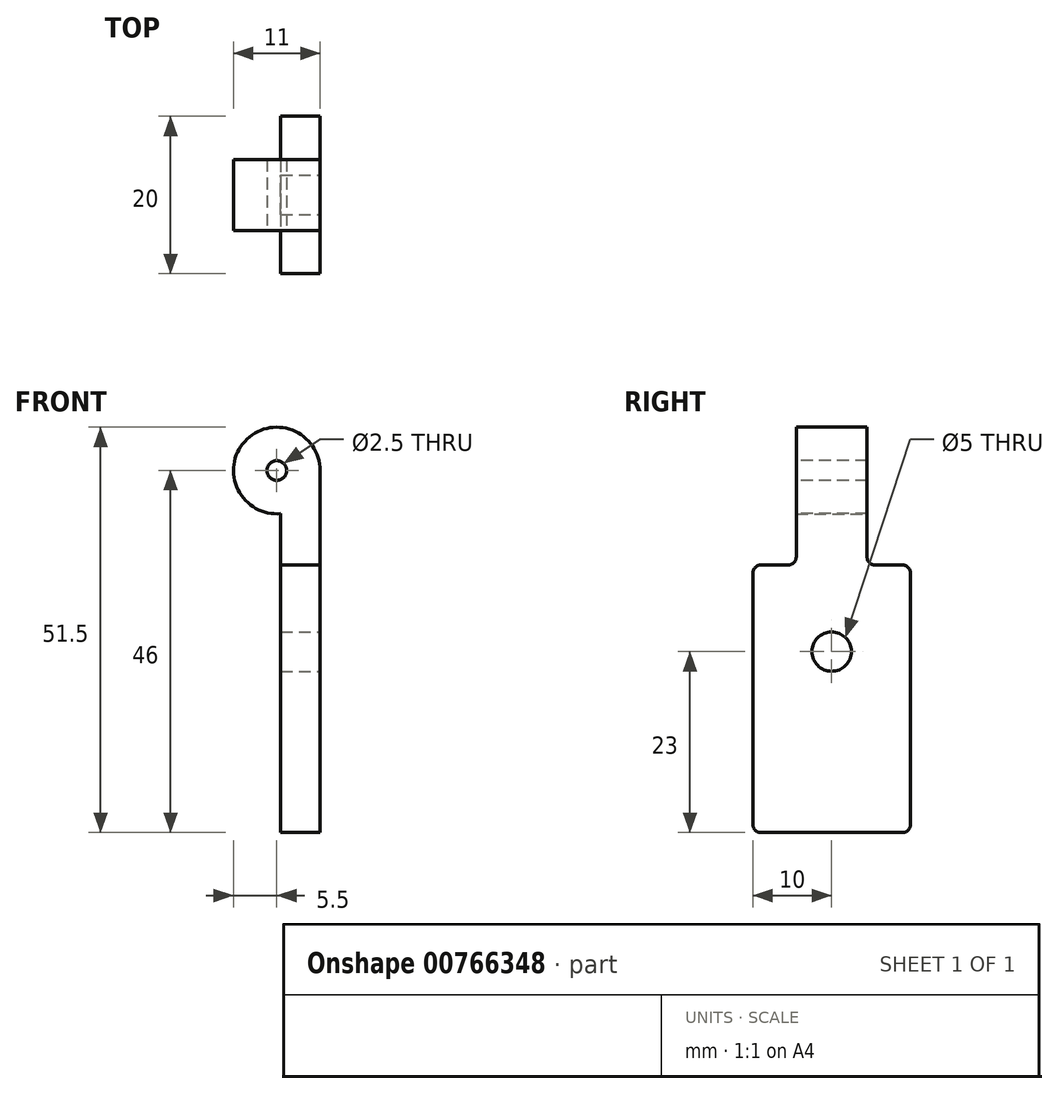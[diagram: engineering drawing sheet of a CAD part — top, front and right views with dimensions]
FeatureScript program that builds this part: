
annotation { "Feature Type Name" : "Feature", "Feature Type Description" : "" }
export const myFeature = defineFeature(function(context is Context, id is Id, definition is map)
    precondition{}
    {
        {
            var Q0;
            Q0=qCreatedBy(makeId("Front.planeOp"),FACE);
            var sketch = newSketch(context, id + "F0", { "sketchPlane" : qUnion([Q0])});
            skCircle(sketch, "E0", {"center": v(0, 0) * mm, "radius": 5.5 * mm});
            skSolve(sketch);
        }
        {
            var Q0;
            Q0 = qSketchRegion(id + "F0", true);
            extrude(context, id + "F1", {"entities" : qUnion([Q0]), "endBound" : BoundingType.SYMMETRIC, "depth" : 9 * mm, "offsetDistance" : 25 * mm});
        }
        {
            var Q0;
            Q0=makeQuery(id+"F1.opExtrude","CAP_FACE",FACE,{"disambiguationData":[OSD([sQuery(id+"F0.wireOp",EDGE,"E0")])],"isStart":false});
            var sketch = newSketch(context, id + "F2", { "sketchPlane" : qUnion([Q0])});
            skLineSegment(sketch, "E1", {"start": v(5.5, 0) * mm, "end": v(5.5, -46) * mm});
            skLineSegment(sketch, "E2", {"start": v(5.5, -46) * mm, "end": v(0.5, -46) * mm});
            skLineSegment(sketch, "E3", {"start": v(0.5, -46) * mm, "end": v(0.5, -5.48) * mm});
            skArc(sketch, "E4.0", {"start": v(0.5, -5.48) * mm, "mid": v(4.06, -3.7) * mm, "end": v(5.5, 0) * mm});
            skSolve(sketch);
        }
        {
            var Q0;
            Q0 = qSketchRegion(id + "F2", true);
            var Q1;
            Q1=makeQuery(id+"F1.opExtrude","CAP_FACE",FACE,{"disambiguationData":[OSD([sQuery(id+"F0.wireOp",EDGE,"E0")])],"isStart":true});
            extrude(context, id + "F3", {"entities" : qUnion([Q0]), "operationType" : NewBodyOperationType.ADD, "endBound" : BoundingType.UP_TO_SURFACE, "oppositeDirection" : true, "depth" : 25 * mm, "endBoundEntityFace" : qUnion([Q1]), "offsetDistance" : 25 * mm});
        }
        {
            var Q0;
            Q0=makeQuery(id+"F3.opExtrude","SWEPT_FACE",FACE,{"disambiguationData":[OSD([sQuery(id+"F2.wireOp",EDGE,"E1")])]});
            var sketch = newSketch(context, id + "F4", { "sketchPlane" : qUnion([Q0])});
            skLineSegment(sketch, "E5", {"start": v(10, -12) * mm, "end": v(-10, -12) * mm});
            skLineSegment(sketch, "E6", {"start": v(-10, -12) * mm, "end": v(-10, -46) * mm});
            skLineSegment(sketch, "E7", {"start": v(-10, -46) * mm, "end": v(10, -46) * mm});
            skLineSegment(sketch, "E8", {"start": v(10, -46) * mm, "end": v(10, -12) * mm});
            skLineSegment(sketch, "E9", {"start": v(-10, -12) * mm, "end": v(0, 0) * mm, "construction": true});
            skLineSegment(sketch, "E10", {"start": v(0, 0) * mm, "end": v(10, -12) * mm, "construction": true});
            skSolve(sketch);
        }
        {
            var Q0;
            Q0 = qSketchRegion(id + "F4", true);
            var Q1;
            Q1=makeQuery(id+"F3.opExtrude","SWEPT_FACE",FACE,{"disambiguationData":[OSD([sQuery(id+"F2.wireOp",EDGE,"E3")])]});
            extrude(context, id + "F5", {"entities" : qUnion([Q0]), "operationType" : NewBodyOperationType.ADD, "endBound" : BoundingType.UP_TO_SURFACE, "oppositeDirection" : true, "depth" : 25 * mm, "endBoundEntityFace" : qUnion([Q1]), "offsetDistance" : 25 * mm});
        }
        {
            var Q0;
            Q0=makeQuery(id+"F3.boolean.opBoolean","MERGE",FACE,{"derivedFrom":[makeQuery(id+"F1.opExtrude","CAP_FACE",FACE,{"disambiguationData":[OSD([sQuery(id+"F0.wireOp",EDGE,"E0")])],"isStart":false}),makeQuery(id+"F3.opExtrude","CAP_FACE",FACE,{"disambiguationData":[OSD([sQuery(id+"F2.wireOp",EDGE,"E1"),sQuery(id+"F2.wireOp",EDGE,"E2"),sQuery(id+"F2.wireOp",EDGE,"E3"),sQuery(id+"F2.wireOp",EDGE,"E4.0")])],"isStart":true})]});
            var sketch = newSketch(context, id + "F6", { "sketchPlane" : qUnion([Q0])});
            skPoint(sketch, "E11", {"position": v(0, 0) * mm});
            skSolve(sketch);
        }
        {
            var Q0;
            Q0=sQuery(id+"F6.wireOp",VERTEX,"E11");
            var Q1;
            Q1=makeQuery(id+"F1.opExtrude","SWEPT_BODY",BODY,{"disambiguationData":[OSD([sQuery(id+"F0.wireOp",EDGE,"E0")])]});
            hole(context, id + "F7", {"style" : HoleStyle.SIMPLE, "endStyle" : HoleEndStyle.THROUGH, "standardTappedOrClearance" : lookupTablePath({ "standard" : "ISO", "engagement" : "75%", "pitch" : "0.5 mm", "size" : "M3", "type" : "Tapped" }), "standardBlindInLast" : lookupTablePath({ "standard" : "ISO", "engagement" : "75%", "pitch" : "0.5 mm", "size" : "M3", "type" : "Tapped" }), "holeDiameter" : 2.5 * mm, "majorDiameter" : 3 * mm, "showTappedDepth" : true, "isTappedThrough" : true, "tappedDepth" : 12 * mm, "tapClearance" : 3, "locations" : qUnion([Q0]), "scope" : qUnion([Q1])});
        }
        {
            var Q0;
            Q0=makeQuery(id+"F5.boolean.opBoolean","MERGE",FACE,{"derivedFrom":[makeQuery(id+"F3.opExtrude","SWEPT_FACE",FACE,{"disambiguationData":[OSD([sQuery(id+"F2.wireOp",EDGE,"E1")])]}),makeQuery(id+"F5.opExtrude","CAP_FACE",FACE,{"disambiguationData":[OSD([sQuery(id+"F4.wireOp",EDGE,"E5"),sQuery(id+"F4.wireOp",EDGE,"E6"),sQuery(id+"F4.wireOp",EDGE,"E7"),sQuery(id+"F4.wireOp",EDGE,"E8")])],"isStart":true})]});
            var sketch = newSketch(context, id + "F8", { "sketchPlane" : qUnion([Q0])});
            skPoint(sketch, "E12", {"position": v(0, -23) * mm});
            skSolve(sketch);
        }
        {
            var Q0;
            Q0=sQuery(id+"F8.wireOp",VERTEX,"E12");
            var Q1;
            Q1=makeQuery(id+"F1.opExtrude","SWEPT_BODY",BODY,{"disambiguationData":[OSD([sQuery(id+"F0.wireOp",EDGE,"E0")])]});
            hole(context, id + "F9", {"style" : HoleStyle.SIMPLE, "endStyle" : HoleEndStyle.THROUGH, "holeDiameter" : 5 * mm, "majorDiameter" : 3 * mm, "isTappedThrough" : true, "tappedDepth" : 12 * mm, "tapClearance" : 3, "locations" : qUnion([Q0]), "scope" : qUnion([Q1])});
        }
        {
            var Q0;
            Q0=makeQuery(id+"F3.opExtrude","SWEPT_EDGE",EDGE,{"disambiguationData":[OSD([sQuery(id+"F0.wireOp",EDGE,"E0"),sQuery(id+"F2.wireOp",EDGE,"E3"),sQuery(id+"F2.wireOp",EDGE,"E4.0")])]});
            var Q1;
            Q1=makeQuery(id+"F5.boolean.opBoolean","INTERSECT",EDGE,{"derivedFrom":[makeQuery(id+"F3.boolean.opBoolean","MERGE",FACE,{"derivedFrom":[makeQuery(id+"F1.opExtrude","CAP_FACE",FACE,{"disambiguationData":[OSD([sQuery(id+"F0.wireOp",EDGE,"E0")])],"isStart":false}),makeQuery(id+"F3.opExtrude","CAP_FACE",FACE,{"disambiguationData":[OSD([sQuery(id+"F2.wireOp",EDGE,"E1"),sQuery(id+"F2.wireOp",EDGE,"E2"),sQuery(id+"F2.wireOp",EDGE,"E3"),sQuery(id+"F2.wireOp",EDGE,"E4.0")])],"isStart":true})]}),makeQuery(id+"F5.opExtrude","SWEPT_FACE",FACE,{"disambiguationData":[OSD([sQuery(id+"F4.wireOp",EDGE,"E5")])]})]});
            var Q2;
            {var subQ0=sQuery(id+"F0.wireOp",EDGE,"E0");Q2=makeQuery(id+"F5.boolean.opBoolean","INTERSECT",EDGE,{"derivedFrom":[makeQuery(id+"F3.boolean.opBoolean","MERGE",FACE,{"derivedFrom":[makeQuery(id+"F1.opExtrude","CAP_FACE",FACE,{"disambiguationData":[OSD([subQ0])],"isStart":true}),makeQuery(id+"F3.opExtrude","CAP_FACE",FACE,{"disambiguationData":[OSD([subQ0])],"isStart":false})]}),makeQuery(id+"F5.opExtrude","SWEPT_FACE",FACE,{"disambiguationData":[OSD([sQuery(id+"F4.wireOp",EDGE,"E5")])]})]});}
            var Q3;
            Q3=makeQuery(id+"F5.opExtrude","SWEPT_EDGE",EDGE,{"disambiguationData":[OSD([sQuery(id+"F4.wireOp",EDGE,"E5"),sQuery(id+"F4.wireOp",EDGE,"E8")])]});
            var Q4;
            Q4=makeQuery(id+"F5.opExtrude","SWEPT_EDGE",EDGE,{"disambiguationData":[OSD([sQuery(id+"F4.wireOp",EDGE,"E5"),sQuery(id+"F4.wireOp",EDGE,"E6")])]});
            var Q5;
            Q5=makeQuery(id+"F5.opExtrude","SWEPT_EDGE",EDGE,{"disambiguationData":[OSD([sQuery(id+"F4.wireOp",EDGE,"E6"),sQuery(id+"F4.wireOp",EDGE,"E7")])]});
            var Q6;
            Q6=makeQuery(id+"F5.opExtrude","SWEPT_EDGE",EDGE,{"disambiguationData":[OSD([sQuery(id+"F4.wireOp",EDGE,"E7"),sQuery(id+"F4.wireOp",EDGE,"E8")])]});
            fillet(context, id + "F10", {"entities" : qUnion([Q0, Q1, Q2, Q3, Q4, Q5, Q6]), "radius" : 1 * mm, "tangentPropagation" : true, "allowEdgeOverflow" : false});
        }
    });
